# Revit family: PD4 AP types Sans hôte
name_source: partatom
category: Dispositifs d'éclairage
units: mm (PartAtom-declared; Revit-internal decimal feet)

## family parameters
Basée sur le plan de construction = Oui
Conserver l'orientation des annotations = Non
Cote de connecteur circulaire = Utiliser le diamètre
Couper avec des vides une fois chargée = Non
Partagée = Non
Point de calcul de pièce = Non
Toujours verticalement = Oui
Type d'élément = Normal

## types (24) — shared parameters
Classe = II
Code d'assemblage = D5010200
Fabricant = B.E.G.
Hauteur de montage max = 350 cm
Image du type = 360°.jpg
Marque = LUXOMAT
Mode de pose = Saillie
URL = http://www.luxomat.com
zero-valued in all types: Elévation par défaut

## per-type parameters (varying)
| type | Alimentation | Charge Cos ɸ =0.5 | Charge Cos ɸ =1 | Charge LED | Commentaires du type | Consommation | IP | Modèle | Relais | Référence | Température ambiante | Type de Sortie |
| 01- PD4 AP Générique | 110-240 V AC |  |  |  | DET.PRES.360°/Ø24M APPARENT |  | 20 ou 54 | PD4 AP |  |  | -25°C à +50°C |  |
| 21- PD4N KNX DX AP réf 93387 | 24 V DC par bus KNX | 0 | 0 | 0 | DET.PRES.KNX.VERSION DELUXE.360°/Ø24M ENCASTRE + KIT AP réf 93307 | 12 mA | 54 | PD4N KNX DX AP | 0 | 93387+93307 | -5°C à +45°C | KNX - 1 sortie Eclairage TOR ou GRADATION / 3 sorties Présence / Capteur de température et bruit |
| 14- PD4 M TRIO DIM AP réf 92730 | 110-240 V AC | 1500 VA | 3000 W | 300 W | DET.PRES.MAITRE.TRIO.2 DIM(1-10V) + TOR.360°/Ø24M APPARENT | 0,78 W | 20 ou 54 | PD4 M TRIO DIM AP | 16 A | 92730 | -25°C à +50°C | 2 DIM (25 ballasts maxi-1er jour/2ème jour) + TOR (Tableau ou CVC) |
| 03- PD4 M 1C AP réf 92580 | 110-240 V AC | 1150 VA | 2300 W | 300 W | DET.PRES.MAITRE.1 CONTACT.360°/Ø24M APPARENT | 0,45 W | 20 ou 54 | PD4 M 1C AP | 10 A | 92580 | -25°C à +50°C | TOR |
| 07- PD4N M DACO AP réf 93460 | 110-240 V AC | 0 | 0 | 0 | DET.PRES.MAITRE.DALI 2.360°/Ø10M APPARENT + KIT AP réf 93465 | 2 W | 54 | PD4N M DACO AP | 0 | 93460+93465 | -25°C à +50°C | DALI 2  (40 drivers maxi) |
| 13- PD4 M DUO DIM AP réf 92271 | 110-240 V AC | 1150 VA | 2300 W | 300 W | DET.PRES.MAITRE.DUO.2 DIM(1-10V).360°/Ø24M APPARENT | 0,50 W | 54 | PD4 M DUO DIM AP | 10 A | 92271 | -25°C à +50°C | 2 DIM (25 ballasts maxi-1er jour/2ème jour) |
| 05- PD4 M 2C DUO AP réf 92158 | 110-240 V AC | 1150 VA | 2300 W | 300 W | DET.PRES.MAITRE.DUO.2 CONTACTS.360°/Ø24M APPARENT | 0,47 W | 54 | PD4 M 2C DUO AP | 10 A | 92158 | -25°C à +50°C | 2  TOR (1er jour/2ème jour) |
| 12- PD4 M DIM AP réf 92147 | 110-240 V AC | 1150 VA | 2300 W | 300 W | DET.PRES.MAITRE.DIM(1-10V).360°/Ø24M APPARENT | 0,50 W | 20 ou 54 | PD4 M DIM AP | 10 A | 92147 | -25°C à +50°C | DIM (50 ballasts maxi) |
| 02- PD4N 1C AP réf 92144 | 110-240 V AC | 1150 VA | 2300 W | 300 W | DET.MOUV.1 CONTACT.360°/Ø24M APPARENT | 0,25 W | 44 | PD4N 1C AP | 10 A | 92144 | -25°C à +50°C | TOR |
| 15- PD4 S AP réf 92142 | 110-240 V AC | 0 | 0 | 0 | DET.PRES.ESCLAVE.360°/Ø24M APPARENT | 0,25 W | 54 | PD4 S AP | 0 | 92142 | -25°C à +50°C | Esclave |
| 04- PD4 M 2C AP réf 92140 | 110-240 V AC | 1150 VA | 2300 W | 300 W | DET.PRES.MAITRE.2 CONTACTS.360°/Ø24M APPARENT | 0,47 W | 54 | PD4 M 2C AP | 10 A / 3 A | 92140 | -25°C à +50°C | TOR + CVC |
| 10- PD4 M DAA4G AP réf 92743 | 110-240 V AC | 1150 VA | 2300 W | 300 W | DET.PRES.MAITRE.DALI ADRESSABLE AUTONOME + TOR.360°/Ø24M APPARENT | 0.4 W | 20 | PD4 M DAA4G AP | 10 A | 92743 | -25°C à +50°C | DALI Adressable Autonome (64 ballasts maxi) + TOR |
| 06- PD4 M 3C TRIO AP réf 92740 | 110-240 V AC | 1500 VA | 3000 W | 300 W | DET.PRES.MAITRE.TRIO.3 CONTACTS.360°/Ø24M APPARENT | 0,58 W | 20 ou 54 | PD4 M 3C TRIO AP | 16 A | 92740 | -25°C à +50°C | 3  TOR (1er jour/2ème jour + Tableau ou CVC) |
| 09- PD4 M TRIO 2DALI/DSI 1C AP réf 92751 | 110-240 V AC | 1500 VA | 3000 W | 300 W | DET.PRES.MAITRE.TRIO.2 DALI/DSI + TOR.360°/Ø24M APPARENT | 0,78 W | 20 ou 54 | PD4 M TRIO 2DALI/DSI 1C AP | 16 A | 92751 | -25°C à +50°C | 2 DALI (25 ballasts maxi-1er jour/2ème jour) + TOR (Tableau ou CVC) |
| 20- PD4N KNX ST AP réf 93385 | 24 V DC par bus KNX | 0 | 0 | 0 | DET.PRES.KNX.VERSION STANDARD.360°/Ø24M ENCASTRE + KIT AP réf 93307 | 12 mA | 54 | PD4N KNX ST AP | 0 | 93385+93307 | -5°C à +45°C | KNX - 1 sortie Eclairage TOR ou GRADATION / 3 sorties Présence |
| 24- PD4N LON AP réf 92834 | 24 V DC par bus LON | 0 | 0 | 0 | DET.PRES.LON.360°/Ø24M APPARENT | 12 mA | 20 ou 54 | PD4N LON AP | 0 | 92834 | -5°C à +45°C | LON |
| 19- PD4N BMS DALI 2 AP réf 93546 | 10-22V DC par bus DALI | 0 | 0 | 0 | MULTI.CAPTEUR.PRES.BMS.DALI 2.360°/Ø24M APPARENT | 7 mA | 54 | PD4N BMS DALI 2 AP | 0 | 93546+93307 | -25°C à +50°C | DALI 2 adressable - BMS |
| 16- PD4 S DAA4G AP réf 92759 | 22 V DC par bus DALI | 0 | 0 | 0 | DET.PRES.ESCLAVE.DALI.360°/Ø24M APPARENT | 7 mA | 54 | PD4 S DAA4G AP | 0 | 92759 | -25°C à +50°C | DALI Esclave |
| 11- PD4 M HCL2 AP réf 93485 | 110-240 V AC | 1150 VA | 2300 W | 300 W | DET.PRES.MAITRE.DALI ADRESSABLE AUTONOME HCL + TOR.360°/Ø24M APPARENT | 0.4 W | 20 | PD4 M HCL2 AP | 10 A | 93485 | -25°C à +50°C | DALI HCL Adressable Autonome (64 ballasts maxi) + TOR |
| 17- PD4N DALILINK AP réf 93377 | 16V DC par bus DALI | 0 | 0 | 0 | MULTI.CAPTEUR.PRES.DALILINK.360°/Ø24M FAUX PLAFOND + KIT AP réf 93307 | 7 mA | 54 | PD4N DALILINK AP | 0 | 93377+93307 | -25°C à +55°C | DALILINK |
| 18- PD4N DALISYS AP réf 93340 | 10-22V DC par bus DALI | 0 | 0 | 0 | MULTI.CAPTEUR.PRES.DALISYS.360°/Ø24M FAUX PLAFOND + KIT AP réf 93307 | 7 mA | 54 | PD4N DALISYS AP | 0 | 93340+93307 | -25°C à +55°C | DALI adressable |
| 08- PD4N M DACO 1C AP réf 93463 | 110-240 V AC | 1150 VA | 2300 W | 300 W | DET.PRES.MAITRE.DALI 2 + CONTACT NO.360°/Ø10M APPARENT + KIT AP réf 93465 | 2 W | 54 | PD4N M DACO 1C AP | 10 A | 93463+93465 | -25°C à +50°C | DALI 2 (40 drivers maxi) + Contact NO |
| 22- PD4N KNXs ST AP réf 93515 | 24 V DC par bus KNX | 0 | 0 | 0 | DET.PRES.KNX Sécure.VERSION STANDARD.360°/Ø24M ENCASTRE + KIT AP réf 93307 | 12 mA | 54 | PD4N KNXs ST AP | 0 | 93515+93307 | -5°C à +45°C | KNX Sécure - 1 sortie Eclairage TOR ou GRADATION / 3 sorties Présence / HCL |
| 23- PD4N KNXs DX AP réf 93517 | 24 V DC par bus KNX | 0 | 0 | 0 | DET.PRES.KNX Sécure.VERSION DELUXE.360°/Ø24M ENCASTRE + KIT AP réf 93307 | 12 mA | 54 | PD4N KNXs DX AP | 0 | 93517+93307 | -5°C à +45°C | KNX Sécure - 1 sortie Eclairage TOR ou GRADATION / 3 sorties Présence / Capteur de température et bruit / HCL |
